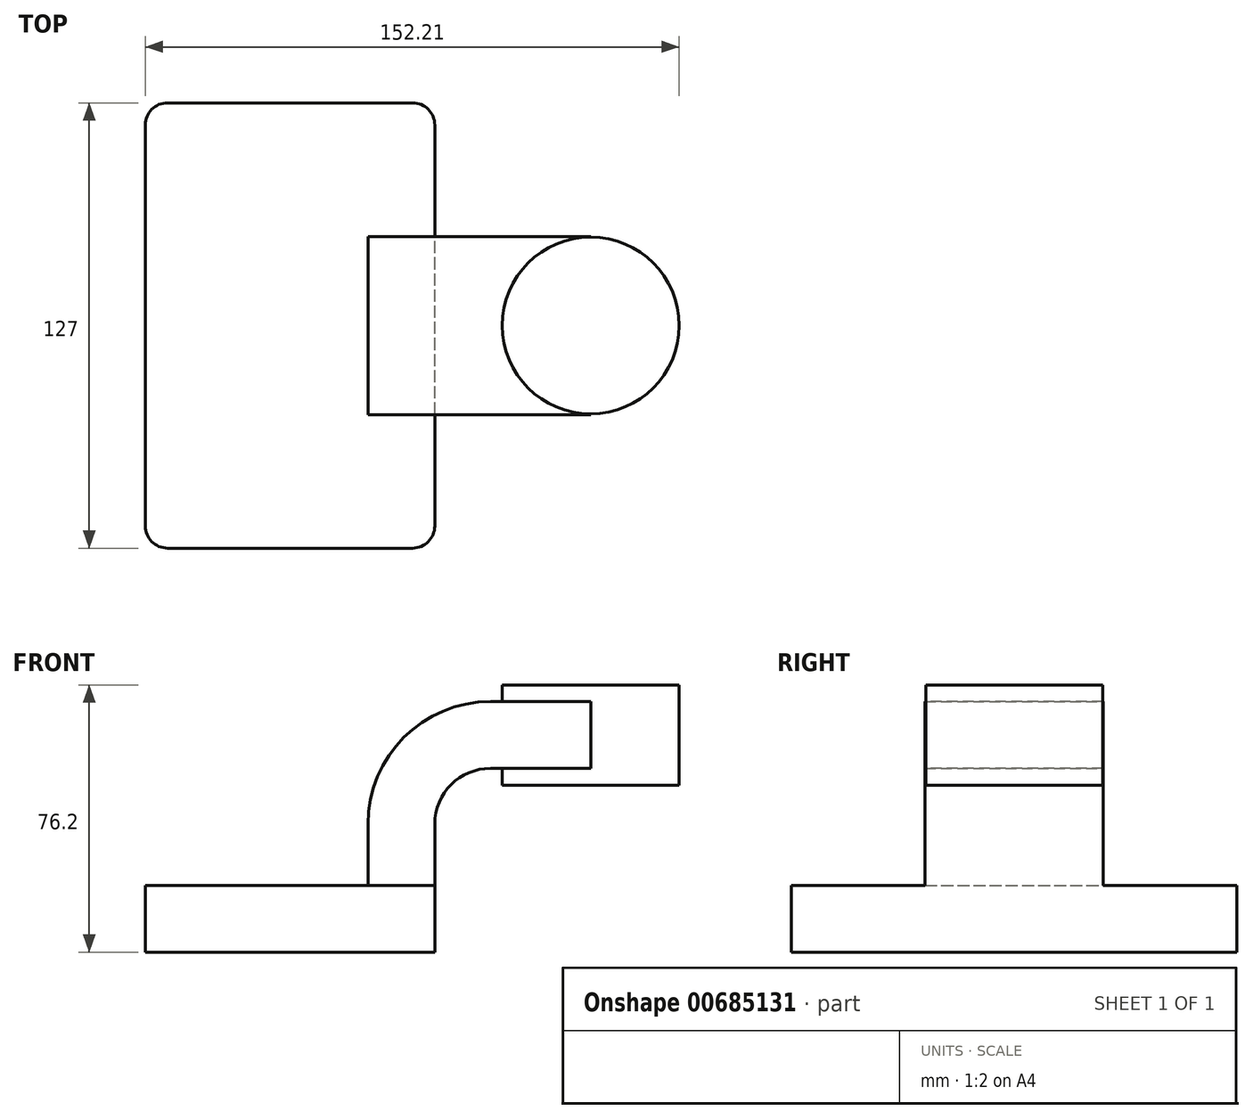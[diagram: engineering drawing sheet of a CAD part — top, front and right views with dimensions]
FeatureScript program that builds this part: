
annotation { "Feature Type Name" : "Feature", "Feature Type Description" : "" }
export const myFeature = defineFeature(function(context is Context, id is Id, definition is map)
    precondition{}
    {
        {
            var Q0;
            Q0=qCreatedBy(makeId("Front.planeOp"),FACE);
            var sketch = newSketch(context, id + "F0", { "sketchPlane" : qUnion([Q0])});
            skLineSegment(sketch, "E0.bottom", {"start": v(-41.28, 4.04) * mm, "end": v(41.28, 4.04) * mm});
            skLineSegment(sketch, "E0.top", {"start": v(-41.28, -15) * mm, "end": v(41.27, -15) * mm});
            skLineSegment(sketch, "E0.left", {"start": v(-41.28, 4.04) * mm, "end": v(-41.28, -15) * mm});
            skLineSegment(sketch, "E0.right", {"start": v(41.28, 4.04) * mm, "end": v(41.27, -15) * mm});
            skPoint(sketch, "E0.middle", {"position": v(0, -5.48) * mm});
            skLineSegment(sketch, "E1.bottom", {"start": v(60.14, 32.62) * mm, "end": v(110.94, 32.62) * mm});
            skLineSegment(sketch, "E1.top", {"start": v(60.14, 61.2) * mm, "end": v(110.94, 61.2) * mm});
            skLineSegment(sketch, "E1.left", {"start": v(60.14, 32.62) * mm, "end": v(60.14, 61.2) * mm});
            skLineSegment(sketch, "E1.right", {"start": v(110.94, 32.62) * mm, "end": v(110.94, 61.2) * mm});
            skPoint(sketch, "E1.middle", {"position": v(85.54, 46.9) * mm});
            skLineSegment(sketch, "E2", {"start": v(41.28, 4.04) * mm, "end": v(41.28, 21.52) * mm});
            skArc(sketch, "E3", {"start": v(41.28, 21.52) * mm, "mid": v(45.92, 32.75) * mm, "end": v(57.15, 37.4) * mm});
            skLineSegment(sketch, "E4", {"start": v(57.15, 37.4) * mm, "end": v(85.72, 37.4) * mm});
            skLineSegment(sketch, "E5.0", {"start": v(57.15, 56.44) * mm, "end": v(85.72, 56.44) * mm});
            skArc(sketch, "E5.1", {"start": v(22.23, 21.52) * mm, "mid": v(32.45, 46.22) * mm, "end": v(57.15, 56.44) * mm});
            skLineSegment(sketch, "E5.2", {"start": v(22.23, 4.04) * mm, "end": v(22.23, 21.52) * mm});
            skFitSpline(sketch, "E6", {"points": [v(-41.28, 4.04) * mm, v(57.15, 56.44) * mm], "startDerivative": vector(0, 67.2) * mm, "endDerivative": vector(131.78, 0) * mm});
            skLineSegment(sketch, "E7", {"start": v(85.72, 61.2) * mm, "end": v(85.72, 32.62) * mm});
            skSolve(sketch);
        }
        {
            var Q0;
            Q0=makeQuery(id+"F0.imprint","IMPRINT",FACE,{"disambiguationData":[TD([[makeQuery(id+"F0.imprint","IMPRINT",EDGE,{"derivedFrom":sQuery(id+"F0.wireOp",EDGE,"E0.top")}),1.0]])]});
            extrude(context, id + "F1", {"entities" : qUnion([Q0]), "endBound" : BoundingType.SYMMETRIC, "depth" : 127 * mm, "offsetDistance" : 25.4 * mm});
        }
        {
            var Q0;
            {var subQ1=sQuery(id+"F0.wireOp",EDGE,"E2");Q0=makeQuery(id+"F0.imprint","IMPRINT",FACE,{"disambiguationData":[TD([[makeQuery(id+"F0.imprint","IMPRINT",EDGE,{"derivedFrom":subQ1}),1.0]])]});}
            var Q1;
            {var subQ5=sQuery(id+"F0.wireOp",EDGE,"o2k5dDIv-ITJZ-lG6F-3pkB-bNVrcg7E1wha");Q1=makeQuery(id+"F0.imprint","IMPRINT",FACE,{"disambiguationData":[TD([[makeQuery(id+"F0.imprint","IMPRINT",EDGE,{"derivedFrom":subQ5}),1.0]])]});}
            var Q2;
            {var subQ0=sQuery(id+"F0.wireOp",EDGE,"E4");var subQ1=sQuery(id+"F0.wireOp",EDGE,"E1.left");var subQ2=makeQuery(id+"F0.imprint","INTERSECT",VERTEX,{"derivedFrom":[subQ1,subQ0]});Q2=makeQuery(id+"F0.imprint","IMPRINT",FACE,{"disambiguationData":[TD([[makeQuery(id+"F0.imprint","IMPRINT",EDGE,{"disambiguationData":[TD([[subQ2,-1.0]])],"derivedFrom":subQ1}),-1.0]])]});}
            extrude(context, id + "F2", {"entities" : qUnion([Q0, Q1, Q2]), "operationType" : NewBodyOperationType.ADD, "endBound" : BoundingType.SYMMETRIC, "depth" : 50.8 * mm, "offsetDistance" : 25.4 * mm});
        }
        {
            var Q0;
            Q0=makeQuery(id+"F0.imprint","IMPRINT",FACE,{"disambiguationData":[TD([[makeQuery(id+"F0.imprint","IMPRINT",EDGE,{"derivedFrom":sQuery(id+"F0.wireOp",EDGE,"E5.1")}),1.0]])]});
            extrude(context, id + "F3", {"entities" : qUnion([Q0]), "operationType" : NewBodyOperationType.ADD, "endBound" : BoundingType.SYMMETRIC, "depth" : 15.88 * mm, "offsetDistance" : 25.4 * mm});
        }
        {
            var Q0;
            {var subQ4=sQuery(id+"F0.wireOp",EDGE,"E1.right");Q0=makeQuery(id+"F0.imprint","IMPRINT",FACE,{"disambiguationData":[TD([[makeQuery(id+"F0.imprint","IMPRINT",EDGE,{"derivedFrom":subQ4}),1.0]])]});}
            var Q1;
            Q1=sQuery(id+"F0.wireOp",EDGE,"E7");
            revolve(context, id + "F4", {"operationType" : NewBodyOperationType.ADD, "surfaceOperationType" : NewSurfaceOperationType.NEW, "entities" : qUnion([Q0]), "axis" : qUnion([Q1]), "revolveType" : RevolveType.FULL});
        }
        {
            var Q0;
            Q0=makeQuery(id+"F1.opExtrude","CAP_EDGE",EDGE,{"disambiguationData":[OSD([sQuery(id+"F0.wireOp",EDGE,"E0.left")])],"isStart":false});
            var Q1;
            Q1=makeQuery(id+"F1.opExtrude","CAP_EDGE",EDGE,{"disambiguationData":[OSD([sQuery(id+"F0.wireOp",EDGE,"E0.right")])],"isStart":false});
            var Q2;
            Q2=makeQuery(id+"F1.opExtrude","CAP_EDGE",EDGE,{"disambiguationData":[OSD([sQuery(id+"F0.wireOp",EDGE,"E0.right")])],"isStart":true});
            var Q3;
            Q3=makeQuery(id+"F1.opExtrude","CAP_EDGE",EDGE,{"disambiguationData":[OSD([sQuery(id+"F0.wireOp",EDGE,"E0.left")])],"isStart":true});
            fillet(context, id + "F5", {"entities" : qUnion([Q0, Q1, Q2, Q3]), "radius" : 6.35 * mm, "tangentPropagation" : true, "allowEdgeOverflow" : false});
        }
    });
